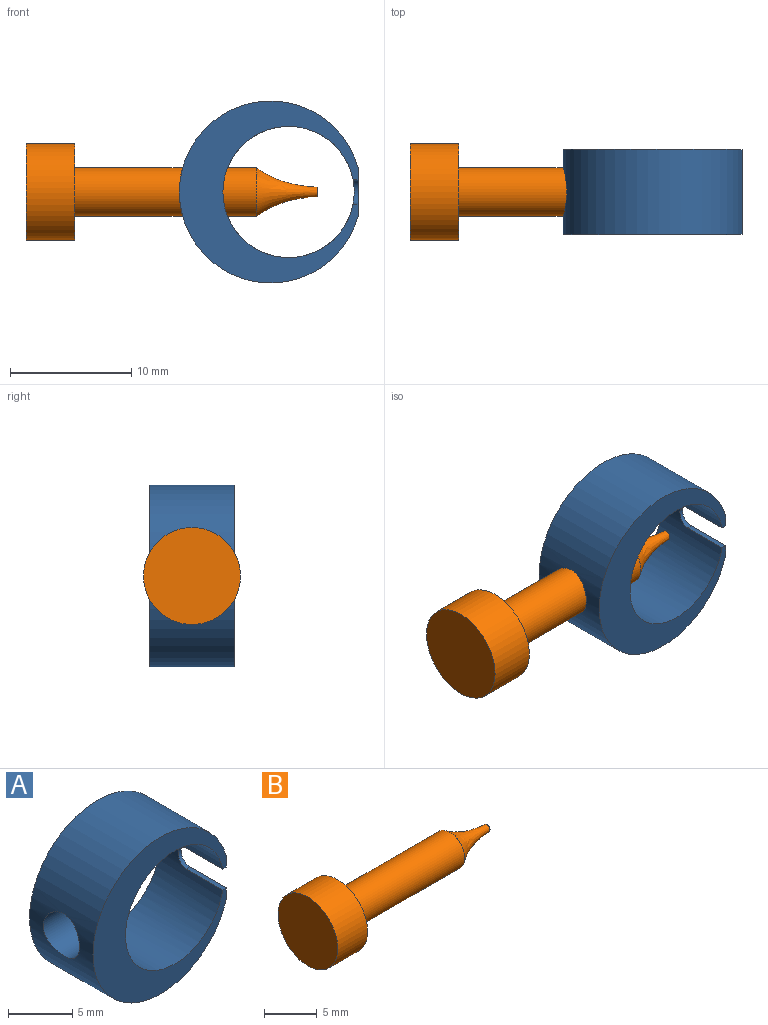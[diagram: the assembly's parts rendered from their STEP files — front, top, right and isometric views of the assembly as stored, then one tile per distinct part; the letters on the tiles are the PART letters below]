
ASSEMBLY  parts=2 mates=1
PART A: 9 faces, bbox 14.7x7x15 mm
  f0: plane 7x4mm, normal (1,0,0), area 18.4mm2, adj f1,f3,f4,f6,f7,f8
  f1: cylinder r=7.5mm len=15mm, axis (0,1,0), area 288.8mm2, adj f0,f3,f4,f5
  f2: cylinder r=5.41mm len=10.82mm, axis (0,1,0), area 215.5mm2, adj f3,f4,f5,f6,f7,f8
  f3: plane 15x14.73mm, normal (0,-1,0), area 83.3mm2, adj f0,f1,f2,f6,f7
  f4: plane 15x14.73mm, normal (0,1,0), area 84mm2, adj f0,f1,f2
  f5: cylinder r=2mm len=4mm, axis (1,0,0), area 45.8mm2, adj f1,f2
  f6: plane 4x0.41mm, normal (0,0,-1), area 1.6mm2, adj f0,f2,f3,f8
  f7: plane 4x0.41mm, normal (0,0,1), area 1.6mm2, adj f0,f2,f3,f8
  f8: cylinder r=1mm len=2mm, axis (1,0,0), area 1.1mm2, adj f0,f2,f6,f7
PART B: 6 faces, bbox 24x8x8 mm
  f0: revolved ~5x4mm, area 31.6mm2, adj f1,f5
  f1: cylinder r=2mm len=15mm, axis (-1,0,0), area 188.5mm2, adj f0,f2
  f2: plane 8x8mm, normal (1,0,0), area 37.7mm2, adj f1,f3
  f3: cylinder r=4mm len=8mm, axis (-1,0,0), area 100.5mm2, adj f2,f4
  f4: plane 8x8mm, normal (-1,0,0), area 50.3mm2, adj f3
  f5: plane 0.8x0.8mm, normal (1,0,0), area 0.5mm2, adj f0
PLACE A t=(-4.49,-0.04,1.46)mm
PLACE B t=(-5.63,-3.54,1.46)mm
MATE slider A.f5 <-> B.f1  axis (1,0,0) through (-10,-3.54,1.46)mm
